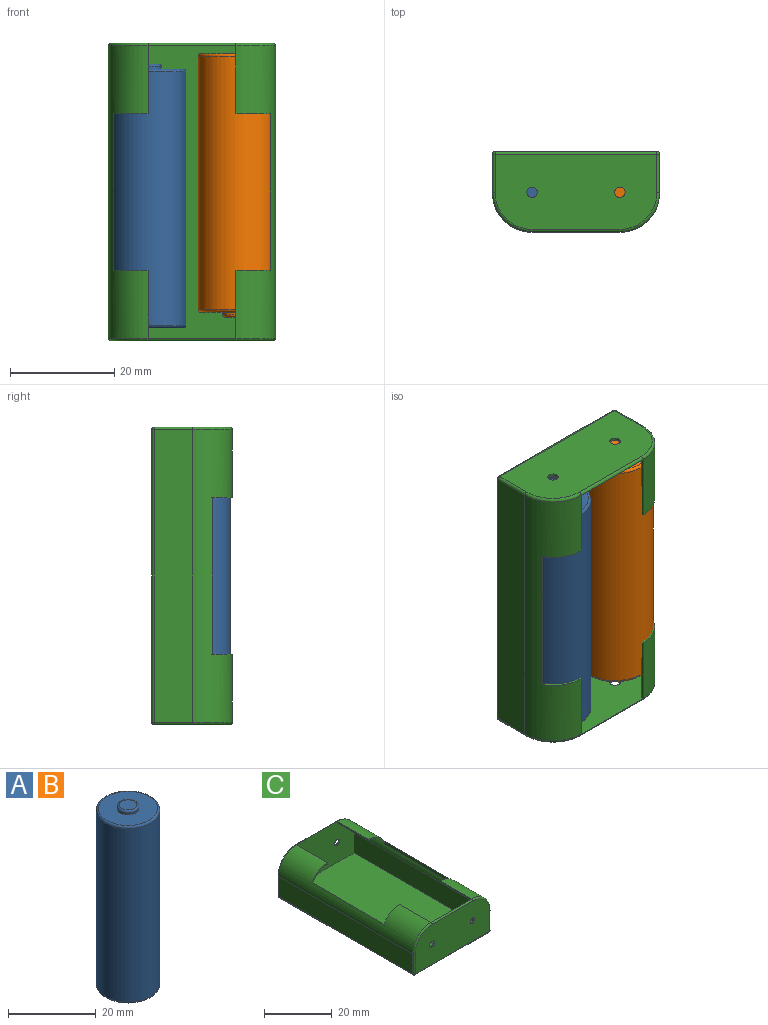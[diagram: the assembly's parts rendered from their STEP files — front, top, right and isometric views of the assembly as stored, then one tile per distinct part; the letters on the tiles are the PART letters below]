
ASSEMBLY  parts=3 mates=2
PART A: 8 faces, bbox 15.7x15.7x50.5 mm
  f0: cylinder r=7.25mm len=48.5mm, axis (0,0,-1), area 2209.3mm2, adj f6,f7
  f1: plane 13.5x13.5mm, normal (0,0,-1), area 143.1mm2, adj f7
  f2: cylinder r=2.5mm len=5mm, axis (0,0,1), area 7.9mm2, adj f3,f5
  f3: plane 13.5x13.5mm, normal (0,0,1), area 123.5mm2, adj f2,f6
  f4: plane 4x4mm, normal (0,0,1), area 12.6mm2, adj f5
  f5: torus R=2mm, axis (0,0,1), area 11.4mm2, adj f2,f4
  f6: torus R=6.75mm, axis (0,0,1), area 34.9mm2, adj f0,f3
  f7: torus R=6.75mm, axis (0,0,1), area 34.9mm2, adj f0,f1
PART B: same geometry as A
PART C: 46 faces, bbox 33.3x57x16 mm
  f0: plane 13x0.5mm, normal (1,0,0), area 6.5mm2, adj f7,f29,f34,f45
  f1: plane 13x0.5mm, normal (-1,0,0), area 6.5mm2, adj f8,f29,f35,f41
  f2: plane 31x14.4mm, normal (0,1,0), area 418.5mm2, adj f14,f18,f21,f22,f24,f26,f37,f39
  f3: plane 56x7.3mm, normal (-1,0,0), area 408.8mm2, adj f7,f10,f14,f15
  f4: plane 31x14.4mm, normal (0,-1,0), area 418.5mm2, adj f9,f10,f11,f13,f16,f17,f36,f38
  f5: plane 56x7.3mm, normal (1,0,0), area 408.8mm2, adj f8,f17,f23,f26
  f6: plane 56x31mm, normal (0,0,-1), area 1736mm2, adj f15,f16,f22,f23
  f7: cylinder r=7.6mm len=56mm, axis (0,1,0), area 428.7mm2, adj f0,f3,f9,f18,f27,f43,f44,f45
  f8: cylinder r=7.6mm len=56mm, axis (0,-1,0), area 428.7mm2, adj f1,f5,f13,f24,f28,f40,f41,f42
  f9: torus R=7.1mm, axis (0,1,0), area 9.2mm2, adj f4,f7,f10,f11
  f10: cylinder r=0.5mm len=7.3mm, axis (0,0,-1), area 5.7mm2, adj f3,f4,f9,f12
  f11: cylinder r=0.5mm len=16.8mm, axis (-1,0,0), area 13.2mm2, adj f4,f9,f13,f31
  f12: sphere r=0.5mm, area 0.4mm2, adj f10,f15,f16
  f13: torus R=7.1mm, axis (0,1,0), area 9.2mm2, adj f4,f8,f11,f17
  f14: cylinder r=0.5mm len=7.3mm, axis (0,0,1), area 5.7mm2, adj f2,f3,f18,f19
  f15: cylinder r=0.5mm len=56mm, axis (0,-1,0), area 44mm2, adj f3,f6,f12,f19
  f16: cylinder r=0.5mm len=31mm, axis (1,0,0), area 24.3mm2, adj f4,f6,f12,f20
  f17: cylinder r=0.5mm len=7.3mm, axis (0,0,1), area 5.7mm2, adj f4,f5,f13,f20
  f18: torus R=7.1mm, axis (0,1,0), area 9.2mm2, adj f2,f7,f14,f21
  f19: sphere r=0.5mm, area 0.4mm2, adj f14,f15,f22
  f20: sphere r=0.5mm, area 0.4mm2, adj f16,f17,f23
  f21: cylinder r=0.5mm len=16.8mm, axis (1,0,0), area 13.2mm2, adj f2,f18,f24,f29
  f22: cylinder r=0.5mm len=31mm, axis (-1,0,0), area 24.3mm2, adj f2,f6,f19,f25
  f23: cylinder r=0.5mm len=56mm, axis (0,1,0), area 44mm2, adj f5,f6,f20,f25
  f24: torus R=7.1mm, axis (0,1,0), area 9.2mm2, adj f2,f8,f21,f26
  f25: sphere r=0.5mm, area 0.4mm2, adj f22,f23,f26
  f26: cylinder r=0.5mm len=7.3mm, axis (0,0,-1), area 5.7mm2, adj f2,f5,f24,f25
  f27: plane 13x0.5mm, normal (1,0,0), area 6.5mm2, adj f7,f31,f34,f44
  f28: plane 13x0.5mm, normal (-1,0,0), area 6.5mm2, adj f8,f31,f35,f42
  f29: plane 31x14.9mm, normal (0,-1,0), area 426.9mm2, adj f0,f1,f21,f30,f32,f33,f34,f35
  f30: plane 56x7.3mm, normal (1,0,0), area 408.8mm2, adj f29,f31,f33,f34
  f31: plane 31x14.9mm, normal (0,1,0), area 426.9mm2, adj f11,f27,f28,f30,f32,f33,f34,f35
  f32: plane 56x7.3mm, normal (-1,0,0), area 408.8mm2, adj f29,f31,f33,f35
  f33: plane 56x31mm, normal (0,0,1), area 1736mm2, adj f29,f30,f31,f32
  f34: cylinder r=7.1mm len=56mm, axis (0,1,0), area 370.4mm2, adj f0,f27,f29,f30,f31,f43,f44,f45
  f35: cylinder r=7.1mm len=56mm, axis (0,-1,0), area 370.4mm2, adj f1,f28,f29,f31,f32,f40,f41,f42
  f36: cylinder r=1mm len=2mm, axis (0,-1,0), area 3.1mm2, adj f4,f31
  f37: cylinder r=1mm len=2mm, axis (0,-1,0), area 3.1mm2, adj f2,f29
  f38: cylinder r=1mm len=2mm, axis (0,-1,0), area 3.1mm2, adj f4,f31
  f39: cylinder r=1mm len=2mm, axis (0,-1,0), area 3.1mm2, adj f2,f29
  f40: plane 30x1.15mm, normal (-1,0,0), area 34.5mm2, adj f8,f35,f41,f42
  f41: plane 6.6x4.98mm, normal (0,-1,0), area 4.1mm2, adj f1,f8,f35,f40
  f42: plane 6.6x4.98mm, normal (0,1,0), area 4.1mm2, adj f8,f28,f35,f40
  f43: plane 30x1.15mm, normal (1,0,0), area 34.5mm2, adj f7,f34,f44,f45
  f44: plane 6.6x4.98mm, normal (0,1,0), area 4.1mm2, adj f7,f27,f34,f43
  f45: plane 6.6x4.98mm, normal (0,-1,0), area 4.1mm2, adj f0,f7,f34,f43
PLACE A t=(-6,6,-23)mm
PLACE B rot(axis=(1,0,0),180deg) t=(10.8,6,29.5)mm
PLACE C rot(axis=(1,0,0),90deg) t=(2.4,13.8,-25.5)mm
MATE fastened C.f7 <-> A.f0  axis (0,0,1) through (-6,6,-25)mm
MATE fastened B.f0 <-> C.f8  axis (0,0,-1) through (10.8,6,29)mm
